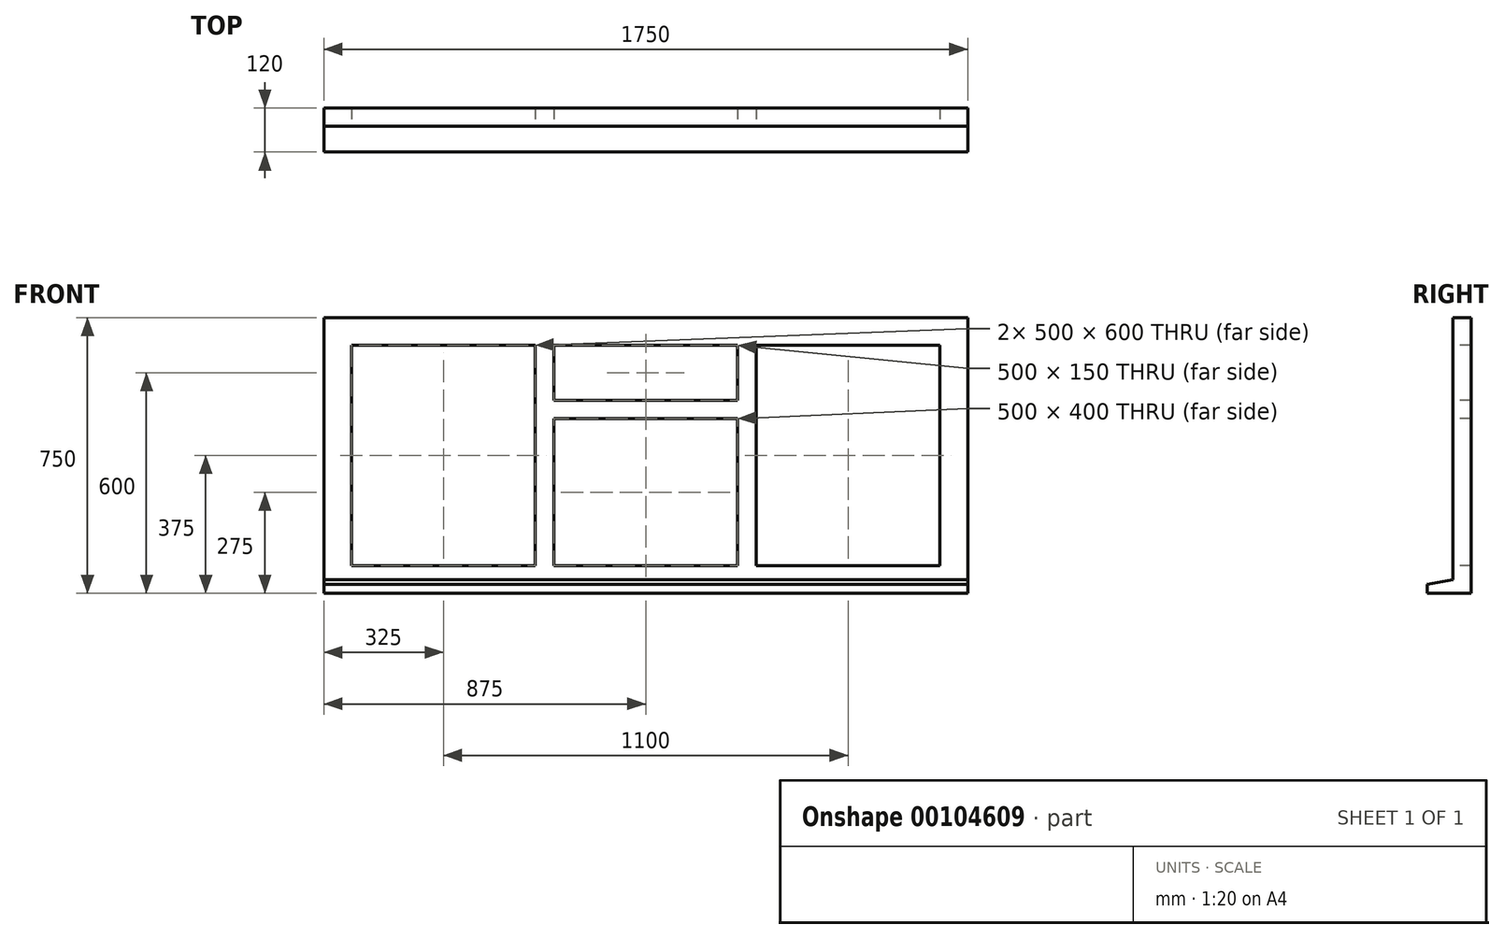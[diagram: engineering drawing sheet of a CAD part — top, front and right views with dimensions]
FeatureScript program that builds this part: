
annotation { "Feature Type Name" : "Feature", "Feature Type Description" : "" }
export const myFeature = defineFeature(function(context is Context, id is Id, definition is map)
    precondition{}
    {
        {
            var Q0;
            Q0=qCreatedBy(makeId("Front.planeOp"),FACE);
            var sketch = newSketch(context, id + "F0", { "sketchPlane" : qUnion([Q0])});
            skLineSegment(sketch, "E0.bottom", {"start": v(0, 0) * mm, "end": v(1750, 0) * mm});
            skLineSegment(sketch, "E0.top", {"start": v(0, -750) * mm, "end": v(1750, -750) * mm});
            skLineSegment(sketch, "E0.left", {"start": v(0, 0) * mm, "end": v(0, -750) * mm});
            skLineSegment(sketch, "E0.right", {"start": v(1750, 0) * mm, "end": v(1750, -750) * mm});
            skLineSegment(sketch, "E1.bottom", {"start": v(1175, -75) * mm, "end": v(1675, -75) * mm});
            skLineSegment(sketch, "E1.top", {"start": v(1175, -675) * mm, "end": v(1675, -675) * mm});
            skLineSegment(sketch, "E1.left", {"start": v(1175, -75) * mm, "end": v(1175, -675) * mm});
            skLineSegment(sketch, "E1.right", {"start": v(1675, -75) * mm, "end": v(1675, -675) * mm});
            skLineSegment(sketch, "E2.bottom", {"start": v(625, -275) * mm, "end": v(1125, -275) * mm});
            skLineSegment(sketch, "E2.top", {"start": v(625, -675) * mm, "end": v(1125, -675) * mm});
            skLineSegment(sketch, "E2.left", {"start": v(625, -275) * mm, "end": v(625, -675) * mm});
            skLineSegment(sketch, "E2.right", {"start": v(1125, -275) * mm, "end": v(1125, -675) * mm});
            skLineSegment(sketch, "E3.bottom", {"start": v(625, -75) * mm, "end": v(1125, -75) * mm});
            skLineSegment(sketch, "E3.top", {"start": v(625, -225) * mm, "end": v(1125, -225) * mm});
            skLineSegment(sketch, "E3.left", {"start": v(625, -75) * mm, "end": v(625, -225) * mm});
            skLineSegment(sketch, "E3.right", {"start": v(1125, -75) * mm, "end": v(1125, -225) * mm});
            skPoint(sketch, "E4.firstSnap0", {"position": v(875, -225) * mm});
            skLineSegment(sketch, "E5", {"start": v(575, -75) * mm, "end": v(575, -675) * mm});
            skLineSegment(sketch, "E6", {"start": v(75, -75) * mm, "end": v(75, -675) * mm});
            skLineSegment(sketch, "E7", {"start": v(575, -75) * mm, "end": v(75, -75) * mm});
            skLineSegment(sketch, "E8", {"start": v(75, -675) * mm, "end": v(575, -675) * mm});
            skSolve(sketch);
        }
        {
            var Q0;
            Q0=qSketchRegion(id+"F0",true);
            extrude(context, id + "F1", {"entities" : qUnion([Q0]), "oppositeDirection" : true, "depth" : 50 * mm});
        }
        {
            var Q0;
            Q0=makeQuery(id+"F1.opExtrude","SWEPT_FACE",FACE,{"disambiguationData":[OSD([sQuery(id+"F0.wireOp",EDGE,"E0.right")])]});
            var sketch = newSketch(context, id + "F2", { "sketchPlane" : qUnion([Q0])});
            skLineSegment(sketch, "E9", {"start": v(0, -750) * mm, "end": v(-70, -750) * mm});
            skLineSegment(sketch, "E10", {"start": v(0, -712.66) * mm, "end": v(-70, -725) * mm});
            skLineSegment(sketch, "E11", {"start": v(-70, -725) * mm, "end": v(-70, -750) * mm});
            skLineSegment(sketch, "E12", {"start": v(0, -750) * mm, "end": v(0, -712.66) * mm});
            skSolve(sketch);
        }
        {
            var Q0;
            Q0=qSketchRegion(id+"F2",true);
            extrude(context, id + "F3", {"entities" : qUnion([Q0]), "operationType" : NewBodyOperationType.ADD, "oppositeDirection" : true, "depth" : 1750 * mm});
        }
    });
